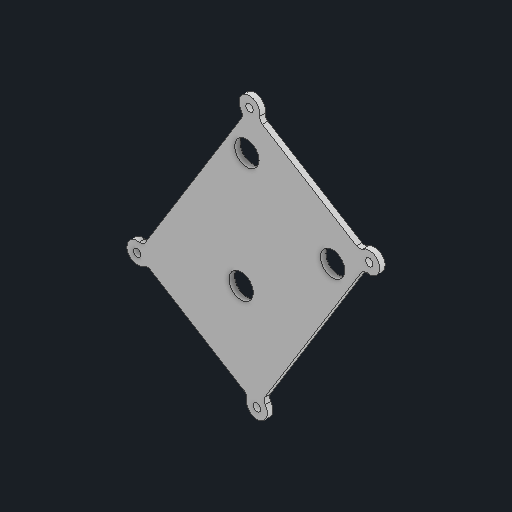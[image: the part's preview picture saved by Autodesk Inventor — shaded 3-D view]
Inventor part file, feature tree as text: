
AUTODESK INVENTOR PART (.ipt)
format: ipt  version: 2024.2 (Build 282272000, 272)  size: 171,008 bytes
history: native  units: in
note: dims shown in document units (in); Inventor stores cm internally (conversion verified against a paired STEP export)
features: reference x8, other x7, extrude x1, fillet x1, sketch x1
ambient origin geometry x8: Origin, YZ Plane, XZ Plane, XY Plane, X Axis, Y Axis, Z Axis, Center Point
bodies: Solid1 (feature_tree)
feature tree (18):
  extrude  "Extrusion1"  Depth=0.125in
  fillet  "Fillet1"  Radius=0.7in
  sketch  "Sketch1"  dims[d0=0.1693in d1=0.7in d2=0.7in d3=0.1693in d4=0.1693in d5=0.1693in d6=1.593in d7=0.4724in d8=0.4724in d9=0.4724in d10=0.4724in d11=0.125in d12=0.0in d13=0.125in]
  reference  "Reference1"
  reference  "Reference2"
  reference  "Reference3"
  reference  "Reference4"
  reference  "Reference5"
  reference  "Reference6"
  reference  "Reference7"
  reference  "Reference8"
  other  "<userpath>\Desktop\Robotics\Swerve2\Assemblies\Pod.iam"
  other  "Pod.iam"
  other  "2800 Series Zinc-Plated Steel Socket Head Screw (M4 x 0.7mm, 7mm Length) - 25 Pack:7"
  other  "2800 Series Zinc-Plated Steel Socket Head Screw (M4 x 0.7mm, 7mm Length) - 25 Pack:5"
  other  "2800 Series Zinc-Plated Steel Socket Head Screw (M4 x 0.7mm, 12mm Length) - 25 Pack:2"
  other  "2800 Series Zinc-Plated Steel Socket Head Screw (M4 x 0.7mm, 12mm Length) - 25 Pack:1"
  other  "Lower_Plate:1"
